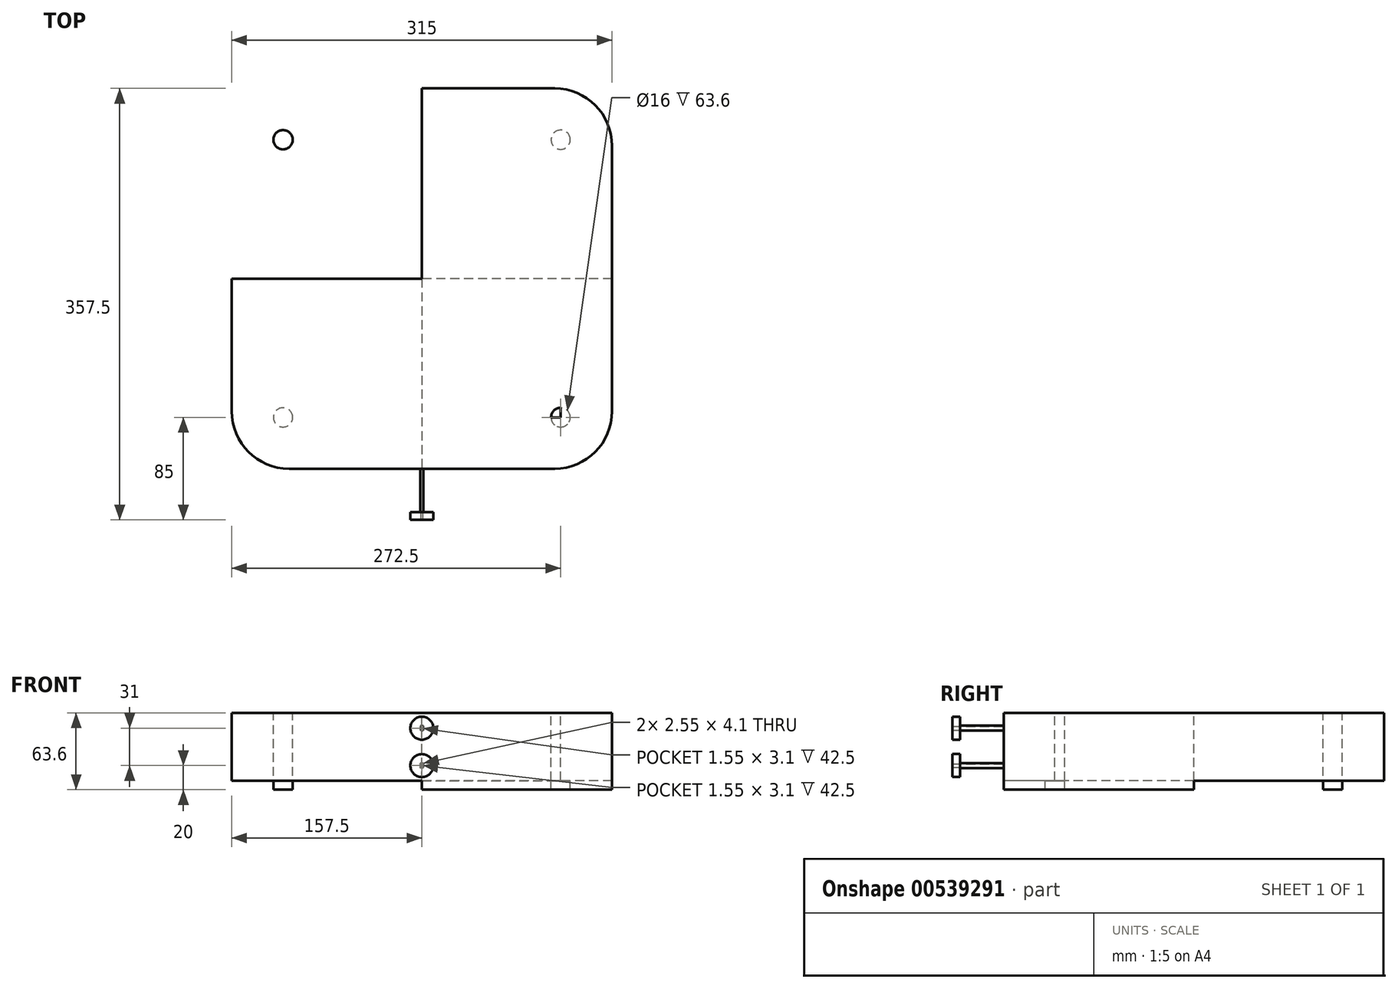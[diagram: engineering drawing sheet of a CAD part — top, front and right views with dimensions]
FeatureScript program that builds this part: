
annotation { "Feature Type Name" : "Feature", "Feature Type Description" : "" }
export const myFeature = defineFeature(function(context is Context, id is Id, definition is map)
    precondition{}
    {
        {
            var Q0;
            Q0=qCreatedBy(makeId("Top.planeOp"),FACE);
            var sketch = newSketch(context, id + "F0", { "sketchPlane" : qUnion([Q0])});
            skLineSegment(sketch, "E0", {"start": v(0, 0) * mm, "end": v(0, -157.5) * mm});
            skLineSegment(sketch, "E1", {"start": v(0, 0) * mm, "end": v(-157.5, 0) * mm});
            skLineSegment(sketch, "E2", {"start": v(-157.5, 0) * mm, "end": v(-157.5, -110) * mm});
            skLineSegment(sketch, "E3", {"start": v(0, -157.5) * mm, "end": v(-110, -157.5) * mm});
            skArc(sketch, "E4", {"start": v(-157.5, -110) * mm, "mid": v(-143.59, -143.59) * mm, "end": v(-110, -157.5) * mm});
            skLineSegment(sketch, "E5", {"start": v(-115, 0) * mm, "end": v(-115, -115) * mm});
            skLineSegment(sketch, "E6", {"start": v(-115, -115) * mm, "end": v(0, -115) * mm});
            skCircle(sketch, "E7", {"center": v(-115, -115) * mm, "radius": 8 * mm});
            skLineSegment(sketch, "E8", {"start": v(175.11, 0) * mm, "end": v(-265.7, 0) * mm});
            skLineSegment(sketch, "E9", {"start": v(0, 142.75) * mm, "end": v(0, -258.92) * mm});
            skPoint(sketch, "E9.endSnap0", {"position": v(0, -78.75) * mm});
            skLineSegment(sketch, "E10.MirrorCS", {"start": v(0, 0) * mm, "end": v(0, 157.5) * mm});
            skArc(sketch, "E11.MirrorCS", {"start": v(-157.5, 110) * mm, "mid": v(-143.59, 143.59) * mm, "end": v(-110, 157.5) * mm});
            skLineSegment(sketch, "E12.MirrorCS", {"start": v(-115, 0) * mm, "end": v(-115, 115) * mm});
            skLineSegment(sketch, "E13.MirrorCS", {"start": v(-115, 115) * mm, "end": v(0, 115) * mm});
            skPoint(sketch, "E14.MirrorP", {"position": v(0, 78.75) * mm});
            skCircle(sketch, "E15.MirrorC", {"center": v(-115, 115) * mm, "radius": 8 * mm});
            skLineSegment(sketch, "E16.MirrorCS", {"start": v(0, 157.5) * mm, "end": v(-110, 157.5) * mm});
            skLineSegment(sketch, "E17.MirrorCS", {"start": v(-157.5, 0) * mm, "end": v(-157.5, 110) * mm});
            skLineSegment(sketch, "E18.MirrorCS", {"start": v(0, 0) * mm, "end": v(157.5, 0) * mm});
            skCircle(sketch, "E19.MirrorC", {"center": v(115, -115) * mm, "radius": 8 * mm});
            skLineSegment(sketch, "E20.MirrorCS", {"start": v(115, 115) * mm, "end": v(0, 115) * mm});
            skLineSegment(sketch, "E21.MirrorCS", {"start": v(157.5, 0) * mm, "end": v(157.5, 110) * mm});
            skLineSegment(sketch, "E22.MirrorCS", {"start": v(115, 0) * mm, "end": v(115, 115) * mm});
            skLineSegment(sketch, "E23.MirrorCS", {"start": v(157.5, 0) * mm, "end": v(157.5, -110) * mm});
            skLineSegment(sketch, "E24.MirrorCS", {"start": v(0, 157.5) * mm, "end": v(110, 157.5) * mm});
            skLineSegment(sketch, "E25.MirrorCS", {"start": v(115, -115) * mm, "end": v(0, -115) * mm});
            skArc(sketch, "E26.MirrorCS", {"start": v(157.5, 110) * mm, "mid": v(143.59, 143.59) * mm, "end": v(110, 157.5) * mm});
            skArc(sketch, "E27.MirrorCS", {"start": v(157.5, -110) * mm, "mid": v(143.59, -143.59) * mm, "end": v(110, -157.5) * mm});
            skCircle(sketch, "E28.MirrorC", {"center": v(115, 115) * mm, "radius": 8 * mm});
            skLineSegment(sketch, "E29.MirrorCS", {"start": v(0, -157.5) * mm, "end": v(110, -157.5) * mm});
            skLineSegment(sketch, "E30.MirrorCS", {"start": v(115, 0) * mm, "end": v(115, -115) * mm});
            skSolve(sketch);
        }
        {
            var Q0;
            {var subQ1=sQuery(id+"F0.wireOp",EDGE,"E23.MirrorCS");Q0=makeQuery(id+"F0.imprint","IMPRINT",FACE,{"disambiguationData":[TD([[makeQuery(id+"F0.imprint","IMPRINT",EDGE,{"derivedFrom":subQ1}),-1.0]])]});}
            var Q1;
            {var subQ5=sQuery(id+"F0.wireOp",EDGE,"E25.MirrorCS");var subQ7=sQuery(id+"F0.wireOp",EDGE,"E19.MirrorC");var subQ8=makeQuery(id+"F0.imprint","INTERSECT",VERTEX,{"derivedFrom":[subQ7,subQ5]});Q1=makeQuery(id+"F0.imprint","IMPRINT",FACE,{"disambiguationData":[TD([[makeQuery(id+"F0.imprint","IMPRINT",EDGE,{"disambiguationData":[TD([[subQ8,-1.0]])],"derivedFrom":subQ7}),1.0]])]});}
            var Q2;
            {var subQ5=sQuery(id+"F0.wireOp",EDGE,"E21.MirrorCS");Q2=makeQuery(id+"F0.imprint","IMPRINT",FACE,{"disambiguationData":[TD([[makeQuery(id+"F0.imprint","IMPRINT",EDGE,{"derivedFrom":subQ5}),1.0]])]});}
            var Q3;
            {var subQ5=sQuery(id+"F0.wireOp",EDGE,"E20.MirrorCS");var subQ7=sQuery(id+"F0.wireOp",EDGE,"E28.MirrorC");var subQ9=makeQuery(id+"F0.imprint","INTERSECT",VERTEX,{"derivedFrom":[subQ5,subQ7]});Q3=makeQuery(id+"F0.imprint","IMPRINT",FACE,{"disambiguationData":[TD([[makeQuery(id+"F0.imprint","IMPRINT",EDGE,{"disambiguationData":[TD([[subQ9,-1.0]])],"derivedFrom":subQ7}),-1.0]])]});}
            var Q4;
            {var subQ0=sQuery(id+"F0.wireOp",EDGE,"E15.MirrorC");var subQ1=sQuery(id+"F0.wireOp",EDGE,"E12.MirrorCS");var subQ2=makeQuery(id+"F0.imprint","INTERSECT",VERTEX,{"derivedFrom":[subQ1,subQ0]});Q4=makeQuery(id+"F0.imprint","IMPRINT",FACE,{"disambiguationData":[TD([[makeQuery(id+"F0.imprint","IMPRINT",EDGE,{"disambiguationData":[TD([[subQ2,1.0]])],"derivedFrom":subQ0}),1.0]])]});}
            var Q5;
            Q5=makeQuery(id+"F0.imprint","IMPRINT",FACE,{"disambiguationData":[TD([[makeQuery(id+"F0.imprint","IMPRINT",EDGE,{"derivedFrom":sQuery(id+"F0.wireOp",EDGE,"E11.MirrorCS")}),-1.0]])]});
            var Q6;
            {var subQ1=sQuery(id+"F0.wireOp",EDGE,"E5");var subQ5=sQuery(id+"F0.wireOp",EDGE,"E7");var subQ6=makeQuery(id+"F0.imprint","INTERSECT",VERTEX,{"derivedFrom":[subQ1,subQ5]});Q6=makeQuery(id+"F0.imprint","IMPRINT",FACE,{"disambiguationData":[TD([[makeQuery(id+"F0.imprint","IMPRINT",EDGE,{"disambiguationData":[TD([[subQ6,1.0]])],"derivedFrom":subQ5}),-1.0]])]});}
            var Q7;
            {var subQ9=sQuery(id+"F0.wireOp",EDGE,"E2");Q7=makeQuery(id+"F0.imprint","IMPRINT",FACE,{"disambiguationData":[TD([[makeQuery(id+"F0.imprint","IMPRINT",EDGE,{"derivedFrom":subQ9}),1.0]])]});}
            var Q8;
            {var subQ0=sQuery(id+"F0.wireOp",EDGE,"E25.MirrorCS");var subQ1=sQuery(id+"F0.wireOp",EDGE,"E19.MirrorC");var subQ2=makeQuery(id+"F0.imprint","INTERSECT",VERTEX,{"derivedFrom":[subQ1,subQ0]});Q8=makeQuery(id+"F0.imprint","IMPRINT",FACE,{"disambiguationData":[TD([[makeQuery(id+"F0.imprint","IMPRINT",EDGE,{"disambiguationData":[TD([[subQ2,1.0]])],"derivedFrom":subQ1}),-1.0]])]});}
            var Q9;
            {var subQ0=sQuery(id+"F0.wireOp",EDGE,"E25.MirrorCS");var subQ1=sQuery(id+"F0.wireOp",EDGE,"E19.MirrorC");var subQ2=makeQuery(id+"F0.imprint","INTERSECT",VERTEX,{"derivedFrom":[subQ1,subQ0]});Q9=makeQuery(id+"F0.imprint","IMPRINT",FACE,{"disambiguationData":[TD([[makeQuery(id+"F0.imprint","IMPRINT",EDGE,{"disambiguationData":[TD([[subQ2,-1.0]])],"derivedFrom":subQ1}),-1.0]])]});}
            var Q10;
            {var subQ0=sQuery(id+"F0.wireOp",EDGE,"E6");var subQ1=sQuery(id+"F0.wireOp",EDGE,"E5");var subQ2=makeQuery(id+"F0.imprint","INTERSECT",VERTEX,{"derivedFrom":[subQ1,subQ0]});Q10=makeQuery(id+"F0.imprint","IMPRINT",FACE,{"disambiguationData":[TD([[makeQuery(id+"F0.imprint","IMPRINT",EDGE,{"disambiguationData":[TD([[subQ2,1.0]])],"derivedFrom":subQ1}),-1.0]])]});}
            var Q11;
            {var subQ0=sQuery(id+"F0.wireOp",EDGE,"E6");var subQ1=sQuery(id+"F0.wireOp",EDGE,"E5");var subQ2=makeQuery(id+"F0.imprint","INTERSECT",VERTEX,{"derivedFrom":[subQ1,subQ0]});Q11=makeQuery(id+"F0.imprint","IMPRINT",FACE,{"disambiguationData":[TD([[makeQuery(id+"F0.imprint","IMPRINT",EDGE,{"disambiguationData":[TD([[subQ2,1.0]])],"derivedFrom":subQ1}),1.0]])]});}
            var Q12;
            {var subQ0=sQuery(id+"F0.wireOp",EDGE,"E22.MirrorCS");var subQ1=sQuery(id+"F0.wireOp",EDGE,"E20.MirrorCS");var subQ2=makeQuery(id+"F0.imprint","INTERSECT",VERTEX,{"derivedFrom":[subQ1,subQ0]});Q12=makeQuery(id+"F0.imprint","IMPRINT",FACE,{"disambiguationData":[TD([[makeQuery(id+"F0.imprint","IMPRINT",EDGE,{"disambiguationData":[TD([[subQ2,-1.0]])],"derivedFrom":subQ1}),-1.0]])]});}
            var Q13;
            {var subQ0=sQuery(id+"F0.wireOp",EDGE,"E22.MirrorCS");var subQ1=sQuery(id+"F0.wireOp",EDGE,"E20.MirrorCS");var subQ2=makeQuery(id+"F0.imprint","INTERSECT",VERTEX,{"derivedFrom":[subQ1,subQ0]});Q13=makeQuery(id+"F0.imprint","IMPRINT",FACE,{"disambiguationData":[TD([[makeQuery(id+"F0.imprint","IMPRINT",EDGE,{"disambiguationData":[TD([[subQ2,-1.0]])],"derivedFrom":subQ1}),1.0]])]});}
            var Q14;
            {var subQ0=sQuery(id+"F0.wireOp",EDGE,"E13.MirrorCS");var subQ1=sQuery(id+"F0.wireOp",EDGE,"E12.MirrorCS");var subQ2=makeQuery(id+"F0.imprint","INTERSECT",VERTEX,{"derivedFrom":[subQ1,subQ0]});Q14=makeQuery(id+"F0.imprint","IMPRINT",FACE,{"disambiguationData":[TD([[makeQuery(id+"F0.imprint","IMPRINT",EDGE,{"disambiguationData":[TD([[subQ2,1.0]])],"derivedFrom":subQ1}),1.0]])]});}
            var Q15;
            {var subQ0=sQuery(id+"F0.wireOp",EDGE,"E13.MirrorCS");var subQ1=sQuery(id+"F0.wireOp",EDGE,"E12.MirrorCS");var subQ2=makeQuery(id+"F0.imprint","INTERSECT",VERTEX,{"derivedFrom":[subQ1,subQ0]});Q15=makeQuery(id+"F0.imprint","IMPRINT",FACE,{"disambiguationData":[TD([[makeQuery(id+"F0.imprint","IMPRINT",EDGE,{"disambiguationData":[TD([[subQ2,1.0]])],"derivedFrom":subQ1}),-1.0]])]});}
            extrude(context, id + "F1", {"entities" : qUnion([Q0, Q1, Q2, Q3, Q4, Q5, Q6, Q7, Q8, Q9, Q10, Q11, Q12, Q13, Q14, Q15]), "endBound" : BoundingType.SYMMETRIC, "oppositeDirection" : true, "depth" : 56.2 * mm, "offsetDistance" : 25 * mm});
        }
        {
            var Q0;
            {var subQ0=sQuery(id+"F0.wireOp",EDGE,"E6");var subQ1=sQuery(id+"F0.wireOp",EDGE,"E5");var subQ2=makeQuery(id+"F0.imprint","INTERSECT",VERTEX,{"derivedFrom":[subQ1,subQ0]});Q0=makeQuery(id+"F0.imprint","IMPRINT",FACE,{"disambiguationData":[TD([[makeQuery(id+"F0.imprint","IMPRINT",EDGE,{"disambiguationData":[TD([[subQ2,1.0]])],"derivedFrom":subQ1}),-1.0]])]});}
            var Q1;
            {var subQ0=sQuery(id+"F0.wireOp",EDGE,"E6");var subQ1=sQuery(id+"F0.wireOp",EDGE,"E5");var subQ2=makeQuery(id+"F0.imprint","INTERSECT",VERTEX,{"derivedFrom":[subQ1,subQ0]});Q1=makeQuery(id+"F0.imprint","IMPRINT",FACE,{"disambiguationData":[TD([[makeQuery(id+"F0.imprint","IMPRINT",EDGE,{"disambiguationData":[TD([[subQ2,1.0]])],"derivedFrom":subQ1}),1.0]])]});}
            var Q2;
            {var subQ0=sQuery(id+"F0.wireOp",EDGE,"E25.MirrorCS");var subQ1=sQuery(id+"F0.wireOp",EDGE,"E19.MirrorC");var subQ2=makeQuery(id+"F0.imprint","INTERSECT",VERTEX,{"derivedFrom":[subQ1,subQ0]});Q2=makeQuery(id+"F0.imprint","IMPRINT",FACE,{"disambiguationData":[TD([[makeQuery(id+"F0.imprint","IMPRINT",EDGE,{"disambiguationData":[TD([[subQ2,1.0]])],"derivedFrom":subQ1}),-1.0]])]});}
            var Q3;
            {var subQ0=sQuery(id+"F0.wireOp",EDGE,"E25.MirrorCS");var subQ1=sQuery(id+"F0.wireOp",EDGE,"E19.MirrorC");var subQ2=makeQuery(id+"F0.imprint","INTERSECT",VERTEX,{"derivedFrom":[subQ1,subQ0]});Q3=makeQuery(id+"F0.imprint","IMPRINT",FACE,{"disambiguationData":[TD([[makeQuery(id+"F0.imprint","IMPRINT",EDGE,{"disambiguationData":[TD([[subQ2,-1.0]])],"derivedFrom":subQ1}),-1.0]])]});}
            var Q4;
            {var subQ0=sQuery(id+"F0.wireOp",EDGE,"E22.MirrorCS");var subQ1=sQuery(id+"F0.wireOp",EDGE,"E20.MirrorCS");var subQ2=makeQuery(id+"F0.imprint","INTERSECT",VERTEX,{"derivedFrom":[subQ1,subQ0]});Q4=makeQuery(id+"F0.imprint","IMPRINT",FACE,{"disambiguationData":[TD([[makeQuery(id+"F0.imprint","IMPRINT",EDGE,{"disambiguationData":[TD([[subQ2,-1.0]])],"derivedFrom":subQ1}),-1.0]])]});}
            var Q5;
            {var subQ0=sQuery(id+"F0.wireOp",EDGE,"E22.MirrorCS");var subQ1=sQuery(id+"F0.wireOp",EDGE,"E20.MirrorCS");var subQ2=makeQuery(id+"F0.imprint","INTERSECT",VERTEX,{"derivedFrom":[subQ1,subQ0]});Q5=makeQuery(id+"F0.imprint","IMPRINT",FACE,{"disambiguationData":[TD([[makeQuery(id+"F0.imprint","IMPRINT",EDGE,{"disambiguationData":[TD([[subQ2,-1.0]])],"derivedFrom":subQ1}),1.0]])]});}
            var Q6;
            {var subQ0=sQuery(id+"F0.wireOp",EDGE,"E13.MirrorCS");var subQ1=sQuery(id+"F0.wireOp",EDGE,"E12.MirrorCS");var subQ2=makeQuery(id+"F0.imprint","INTERSECT",VERTEX,{"derivedFrom":[subQ1,subQ0]});Q6=makeQuery(id+"F0.imprint","IMPRINT",FACE,{"disambiguationData":[TD([[makeQuery(id+"F0.imprint","IMPRINT",EDGE,{"disambiguationData":[TD([[subQ2,1.0]])],"derivedFrom":subQ1}),1.0]])]});}
            var Q7;
            {var subQ0=sQuery(id+"F0.wireOp",EDGE,"E13.MirrorCS");var subQ1=sQuery(id+"F0.wireOp",EDGE,"E12.MirrorCS");var subQ2=makeQuery(id+"F0.imprint","INTERSECT",VERTEX,{"derivedFrom":[subQ1,subQ0]});Q7=makeQuery(id+"F0.imprint","IMPRINT",FACE,{"disambiguationData":[TD([[makeQuery(id+"F0.imprint","IMPRINT",EDGE,{"disambiguationData":[TD([[subQ2,1.0]])],"derivedFrom":subQ1}),-1.0]])]});}
            extrude(context, id + "F2", {"entities" : qUnion([Q0, Q1, Q2, Q3, Q4, Q5, Q6, Q7]), "operationType" : NewBodyOperationType.ADD, "oppositeDirection" : true, "depth" : 35.5 * mm, "offsetDistance" : 25 * mm});
        }
        {
            var Q0;
            Q0=makeQuery(id+"F1.opExtrude","SWEPT_FACE",FACE,{"disambiguationData":[OSD([sQuery(id+"F0.wireOp",EDGE,"E3"),sQuery(id+"F0.wireOp",EDGE,"E29.MirrorCS")])]});
            var sketch = newSketch(context, id + "F3", { "sketchPlane" : qUnion([Q0])});
            skLineSegment(sketch, "E31", {"start": v(0, 0) * mm, "end": v(110, 0) * mm});
            skLineSegment(sketch, "E32", {"start": v(0, -15.5) * mm, "end": v(110, -15.5) * mm});
            skLineSegment(sketch, "E33", {"start": v(0, -15.5) * mm, "end": v(0, 0) * mm});
            skLineSegment(sketch, "E34.bottom", {"start": v(-0.77, -13.95) * mm, "end": v(0.78, -13.95) * mm});
            skLineSegment(sketch, "E34.top", {"start": v(-0.77, -17.05) * mm, "end": v(0.78, -17.05) * mm});
            skLineSegment(sketch, "E34.left", {"start": v(-0.77, -13.95) * mm, "end": v(-0.77, -17.05) * mm});
            skLineSegment(sketch, "E34.right", {"start": v(0.78, -13.95) * mm, "end": v(0.78, -17.05) * mm});
            skPoint(sketch, "E34.middle", {"position": v(0, -15.5) * mm});
            skLineSegment(sketch, "E35.bottom", {"start": v(1.28, -17.55) * mm, "end": v(-1.27, -17.55) * mm});
            skLineSegment(sketch, "E35.top", {"start": v(1.28, -13.45) * mm, "end": v(-1.27, -13.45) * mm});
            skLineSegment(sketch, "E35.left", {"start": v(1.28, -17.55) * mm, "end": v(1.28, -13.45) * mm});
            skLineSegment(sketch, "E35.right", {"start": v(-1.27, -17.55) * mm, "end": v(-1.27, -13.45) * mm});
            skPoint(sketch, "E36.MirrorP", {"position": v(0, 15.5) * mm});
            skLineSegment(sketch, "E37.MirrorCS", {"start": v(0, 15.5) * mm, "end": v(110, 15.5) * mm});
            skLineSegment(sketch, "E38.MirrorCS", {"start": v(0, 15.5) * mm, "end": v(0, 0) * mm});
            skLineSegment(sketch, "E39.MirrorCS", {"start": v(-0.77, 13.95) * mm, "end": v(0.78, 13.95) * mm});
            skLineSegment(sketch, "E40.MirrorCS", {"start": v(-0.77, 17.05) * mm, "end": v(0.78, 17.05) * mm});
            skLineSegment(sketch, "E41.MirrorCS", {"start": v(-0.77, 13.95) * mm, "end": v(-0.77, 17.05) * mm});
            skLineSegment(sketch, "E42.MirrorCS", {"start": v(0.78, 13.95) * mm, "end": v(0.78, 17.05) * mm});
            skLineSegment(sketch, "E43.MirrorCS", {"start": v(1.28, 13.45) * mm, "end": v(-1.27, 13.45) * mm});
            skLineSegment(sketch, "E44.MirrorCS", {"start": v(-1.27, 17.55) * mm, "end": v(-1.27, 13.45) * mm});
            skLineSegment(sketch, "E45.MirrorCS", {"start": v(1.28, 17.55) * mm, "end": v(-1.27, 17.55) * mm});
            skLineSegment(sketch, "E46.MirrorCS", {"start": v(1.28, 17.55) * mm, "end": v(1.28, 13.45) * mm});
            skSolve(sketch);
        }
        {
            var Q0;
            {var subQ0=sQuery(id+"F3.wireOp",EDGE,"E34.top");Q0=makeQuery(id+"F3.imprint","IMPRINT",FACE,{"disambiguationData":[TD([[makeQuery(id+"F3.imprint","IMPRINT",EDGE,{"derivedFrom":subQ0}),-1.0]])]});}
            var Q1;
            {var subQ0=sQuery(id+"F3.wireOp",EDGE,"E34.right");var subQ3=sQuery(id+"F3.wireOp",EDGE,"E32");var subQ4=makeQuery(id+"F3.imprint","INTERSECT",VERTEX,{"derivedFrom":[subQ3,subQ0]});Q1=makeQuery(id+"F3.imprint","IMPRINT",FACE,{"disambiguationData":[TD([[makeQuery(id+"F3.imprint","IMPRINT",EDGE,{"disambiguationData":[TD([[subQ4,-1.0]])],"derivedFrom":subQ3}),1.0]])]});}
            var Q2;
            {var subQ0=sQuery(id+"F3.wireOp",EDGE,"E40.MirrorCS");Q2=makeQuery(id+"F3.imprint","IMPRINT",FACE,{"disambiguationData":[TD([[makeQuery(id+"F3.imprint","IMPRINT",EDGE,{"derivedFrom":subQ0}),1.0]])]});}
            var Q3;
            {var subQ0=sQuery(id+"F3.wireOp",EDGE,"E42.MirrorCS");var subQ3=sQuery(id+"F3.wireOp",EDGE,"E37.MirrorCS");var subQ4=makeQuery(id+"F3.imprint","INTERSECT",VERTEX,{"derivedFrom":[subQ3,subQ0]});Q3=makeQuery(id+"F3.imprint","IMPRINT",FACE,{"disambiguationData":[TD([[makeQuery(id+"F3.imprint","IMPRINT",EDGE,{"disambiguationData":[TD([[subQ4,-1.0]])],"derivedFrom":subQ3}),-1.0]])]});}
            extrude(context, id + "F4", {"entities" : qUnion([Q0, Q1, Q2, Q3]), "operationType" : NewBodyOperationType.ADD, "depth" : 42.5 * mm, "offsetDistance" : 25 * mm});
        }
        {
            var Q0;
            Q0=makeQuery(id+"F4.opExtrude","CAP_FACE",FACE,{"disambiguationData":[OSD([sQuery(id+"F3.wireOp",EDGE,"E39.MirrorCS"),sQuery(id+"F3.wireOp",EDGE,"E40.MirrorCS"),sQuery(id+"F3.wireOp",EDGE,"E41.MirrorCS"),sQuery(id+"F3.wireOp",EDGE,"E42.MirrorCS"),sQuery(id+"F3.wireOp",EDGE,"E43.MirrorCS"),sQuery(id+"F3.wireOp",EDGE,"E44.MirrorCS"),sQuery(id+"F3.wireOp",EDGE,"E45.MirrorCS"),sQuery(id+"F3.wireOp",EDGE,"E46.MirrorCS")])],"isStart":false});
            var sketch = newSketch(context, id + "F5", { "sketchPlane" : qUnion([Q0])});
            skLineSegment(sketch, "E47", {"start": v(-1.27, 15.5) * mm, "end": v(1.28, 15.5) * mm});
            skLineSegment(sketch, "E48", {"start": v(0, 17.55) * mm, "end": v(0, 13.45) * mm});
            skCircle(sketch, "E49", {"center": v(0, 15.5) * mm, "radius": 9.53 * mm});
            skSolve(sketch);
        }
        {
            var Q0;
            Q0=makeQuery(id+"F5.imprint","IMPRINT",FACE,{"disambiguationData":[TD([[makeQuery(id+"F5.imprint","IMPRINT",EDGE,{"derivedFrom":sQuery(id+"F5.wireOp",EDGE,"E49")}),1.0]])]});
            extrude(context, id + "F6", {"entities" : qUnion([Q0]), "operationType" : NewBodyOperationType.ADD, "oppositeDirection" : true, "depth" : 6.35 * mm, "offsetDistance" : 25 * mm});
        }
        {
            var Q0;
            Q0=makeQuery(id+"F4.opExtrude","CAP_FACE",FACE,{"disambiguationData":[OSD([sQuery(id+"F3.wireOp",EDGE,"E34.bottom"),sQuery(id+"F3.wireOp",EDGE,"E34.top"),sQuery(id+"F3.wireOp",EDGE,"E34.left"),sQuery(id+"F3.wireOp",EDGE,"E34.right"),sQuery(id+"F3.wireOp",EDGE,"E35.bottom"),sQuery(id+"F3.wireOp",EDGE,"E35.top"),sQuery(id+"F3.wireOp",EDGE,"E35.left"),sQuery(id+"F3.wireOp",EDGE,"E35.right")])],"isStart":false});
            var sketch = newSketch(context, id + "F7", { "sketchPlane" : qUnion([Q0])});
            skLineSegment(sketch, "E50", {"start": v(-1.27, -15.5) * mm, "end": v(1.28, -15.5) * mm});
            skLineSegment(sketch, "E51", {"start": v(0, -13.45) * mm, "end": v(0, -17.55) * mm});
            skCircle(sketch, "E52", {"center": v(0, -15.5) * mm, "radius": 9.53 * mm});
            skSolve(sketch);
        }
        {
            var Q0;
            Q0=makeQuery(id+"F7.imprint","IMPRINT",FACE,{"disambiguationData":[TD([[makeQuery(id+"F7.imprint","IMPRINT",EDGE,{"derivedFrom":sQuery(id+"F7.wireOp",EDGE,"E52")}),1.0]])]});
            extrude(context, id + "F8", {"entities" : qUnion([Q0]), "operationType" : NewBodyOperationType.ADD, "oppositeDirection" : true, "depth" : 6.35 * mm, "offsetDistance" : 25 * mm});
        }
    });
